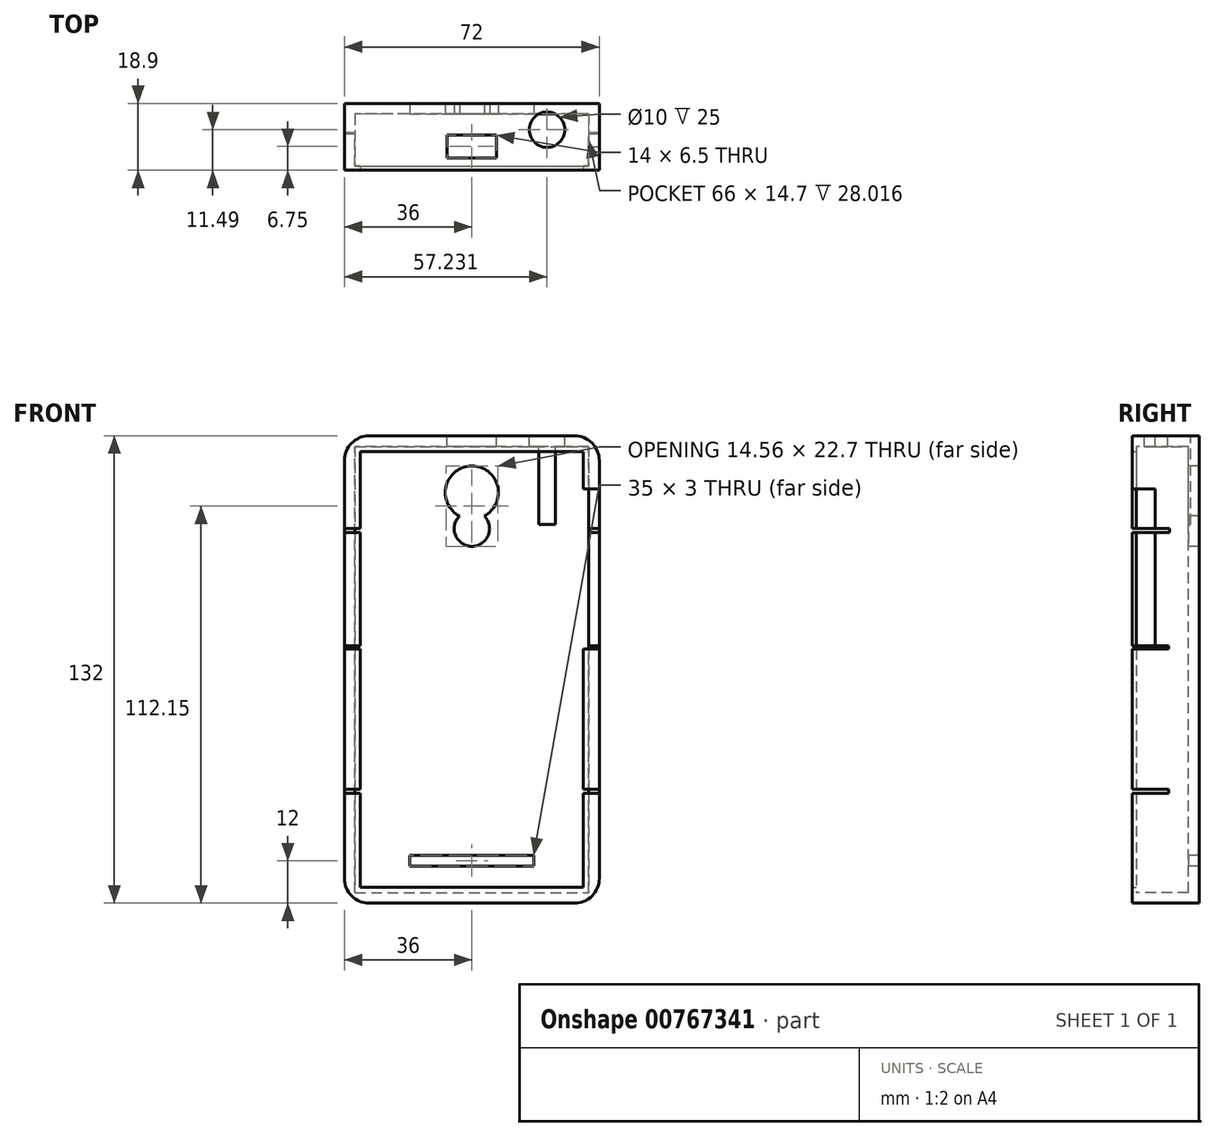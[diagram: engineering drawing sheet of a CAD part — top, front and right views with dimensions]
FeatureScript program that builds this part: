
annotation { "Feature Type Name" : "Feature", "Feature Type Description" : "" }
export const myFeature = defineFeature(function(context is Context, id is Id, definition is map)
    precondition{}
    {
        {
            var Q0;
            Q0=qCreatedBy(makeId("Front.planeOp"),FACE);
            var sketch = newSketch(context, id + "F0", { "sketchPlane" : qUnion([Q0])});
            skPoint(sketch, "E0.0", {"position": v(0, 0) * mm});
            skLineSegment(sketch, "E1.bottom", {"start": v(-36, 66) * mm, "end": v(36, 66) * mm});
            skLineSegment(sketch, "E1.top", {"start": v(-36, -66) * mm, "end": v(36, -66) * mm});
            skLineSegment(sketch, "E1.left", {"start": v(-36, 66) * mm, "end": v(-36, -66) * mm});
            skLineSegment(sketch, "E1.right", {"start": v(36, 66) * mm, "end": v(36, -66) * mm});
            skSolve(sketch);
        }
        {
            var Q0;
            Q0=makeQuery(id+"F0.imprint","IMPRINT",FACE,{"disambiguationData":[TD([[makeQuery(id+"F0.imprint","IMPRINT",EDGE,{"derivedFrom":sQuery(id+"F0.wireOp",EDGE,"E1.bottom")}),-1.0]])]});
            extrude(context, id + "F1", {"entities" : qUnion([Q0]), "depth" : 17.7 * mm, "offsetDistance" : 25 * mm});
        }
        {
            var Q0;
            Q0=makeQuery(id+"F1.opExtrude","CAP_FACE",FACE,{"disambiguationData":[OSD([sQuery(id+"F0.wireOp",EDGE,"E1.bottom"),sQuery(id+"F0.wireOp",EDGE,"E1.top"),sQuery(id+"F0.wireOp",EDGE,"E1.left"),sQuery(id+"F0.wireOp",EDGE,"E1.right")])],"isStart":false});
            var sketch = newSketch(context, id + "F2", { "sketchPlane" : qUnion([Q0])});
            skLineSegment(sketch, "E2.bottom", {"start": v(-33, 63) * mm, "end": v(33, 63) * mm});
            skLineSegment(sketch, "E2.top", {"start": v(-33, -63) * mm, "end": v(33, -63) * mm});
            skLineSegment(sketch, "E2.left", {"start": v(-33, 63) * mm, "end": v(-33, -63) * mm});
            skLineSegment(sketch, "E2.right", {"start": v(33, 63) * mm, "end": v(33, -63) * mm});
            skSolve(sketch);
        }
        {
            var Q0;
            Q0=makeQuery(id+"F2.imprint","IMPRINT",FACE,{"disambiguationData":[TD([[makeQuery(id+"F2.imprint","IMPRINT",EDGE,{"derivedFrom":sQuery(id+"F2.wireOp",EDGE,"E2.bottom")}),-1.0]])]});
            var Q1;
            Q1=makeQuery(id+"F1.opExtrude","CAP_FACE",FACE,{"disambiguationData":[OSD([sQuery(id+"F0.wireOp",EDGE,"E1.bottom"),sQuery(id+"F0.wireOp",EDGE,"E1.top"),sQuery(id+"F0.wireOp",EDGE,"E1.left"),sQuery(id+"F0.wireOp",EDGE,"E1.right")])],"isStart":true});
            extrude(context, id + "F3", {"entities" : qUnion([Q0]), "operationType" : NewBodyOperationType.REMOVE, "endBound" : BoundingType.UP_TO_SURFACE, "oppositeDirection" : true, "depth" : 8.5 * mm, "endBoundEntityFace" : qUnion([Q1]), "hasOffset" : true, "offsetDistance" : 3 * mm});
        }
        {
            var Q0;
            Q0=makeQuery(id+"F1.opExtrude","CAP_FACE",FACE,{"disambiguationData":[OSD([sQuery(id+"F0.wireOp",EDGE,"E1.bottom"),sQuery(id+"F0.wireOp",EDGE,"E1.top"),sQuery(id+"F0.wireOp",EDGE,"E1.left"),sQuery(id+"F0.wireOp",EDGE,"E1.right")])],"isStart":false});
            var sketch = newSketch(context, id + "F4", { "sketchPlane" : qUnion([Q0])});
            skLineSegment(sketch, "E3.bottom", {"start": v(-31.5, 61.5) * mm, "end": v(31.5, 61.5) * mm});
            skLineSegment(sketch, "E3.top", {"start": v(-31.5, -61.5) * mm, "end": v(31.5, -61.5) * mm});
            skLineSegment(sketch, "E3.left", {"start": v(-31.5, 61.5) * mm, "end": v(-31.5, -61.5) * mm});
            skLineSegment(sketch, "E3.right", {"start": v(31.5, 61.5) * mm, "end": v(31.5, -61.5) * mm});
            skSolve(sketch);
        }
        {
            var Q0;
            Q0=makeQuery(id+"F4.imprint","IMPRINT",FACE,{"disambiguationData":[TD([[makeQuery(id+"F4.imprint","IMPRINT",EDGE,{"derivedFrom":sQuery(id+"F4.wireOp",EDGE,"E3.bottom")}),1.0]])]});
            var Q1;
            Q1=makeQuery(id+"F4.imprint","IMPRINT",FACE,{"disambiguationData":[TD([[makeQuery(id+"F4.imprint","IMPRINT",EDGE,{"derivedFrom":makeQuery(id+"F1.opExtrude","CAP_EDGE",EDGE,{"disambiguationData":[OSD([sQuery(id+"F0.wireOp",EDGE,"E1.bottom")])],"isStart":false})}),-1.0]])]});
            extrude(context, id + "F5", {"entities" : qUnion([Q0, Q1]), "operationType" : NewBodyOperationType.ADD, "depth" : 1.2 * mm, "offsetDistance" : 25 * mm});
        }
        {
            var Q0;
            Q0=makeQuery(id+"F3.boolean.opBoolean","COPY",FACE,{"derivedFrom":makeQuery(id+"F3.opExtrude","CAP_FACE",FACE,{"disambiguationData":[OSD([sQuery(id+"F2.wireOp",EDGE,"E2.bottom"),sQuery(id+"F2.wireOp",EDGE,"E2.top"),sQuery(id+"F2.wireOp",EDGE,"E2.left"),sQuery(id+"F2.wireOp",EDGE,"E2.right")])],"isStart":false})});
            var sketch = newSketch(context, id + "F6", { "sketchPlane" : qUnion([Q0])});
            skCircle(sketch, "E4", {"center": v(0, 50) * mm, "radius": 7.5 * mm});
            skSolve(sketch);
        }
        {
            var Q0;
            Q0=makeQuery(id+"F6.imprint","IMPRINT",FACE,{"disambiguationData":[TD([[makeQuery(id+"F6.imprint","IMPRINT",EDGE,{"derivedFrom":sQuery(id+"F6.wireOp",EDGE,"E4")}),1.0]])]});
            extrude(context, id + "F7", {"entities" : qUnion([Q0]), "operationType" : NewBodyOperationType.REMOVE, "oppositeDirection" : true, "depth" : 25 * mm, "offsetDistance" : 25 * mm});
        }
        {
            var Q0;
            Q0 = qSketchRegion(id + "F6", true);
            extrude(context, id + "F8", {"entities" : qUnion([Q0]), "operationType" : NewBodyOperationType.REMOVE, "oppositeDirection" : true, "depth" : 25 * mm, "offsetDistance" : 25 * mm});
        }
        {
            var Q0;
            Q0=makeQuery(id+"F3.boolean.opBoolean","COPY",FACE,{"derivedFrom":makeQuery(id+"F3.opExtrude","CAP_FACE",FACE,{"disambiguationData":[OSD([sQuery(id+"F2.wireOp",EDGE,"E2.bottom"),sQuery(id+"F2.wireOp",EDGE,"E2.top"),sQuery(id+"F2.wireOp",EDGE,"E2.left"),sQuery(id+"F2.wireOp",EDGE,"E2.right")])],"isStart":false})});
            var sketch = newSketch(context, id + "F9", { "sketchPlane" : qUnion([Q0])});
            skCircle(sketch, "E5", {"center": v(0, 39.8) * mm, "radius": 5 * mm});
            skSolve(sketch);
        }
        {
            var Q0;
            Q0 = qSketchRegion(id + "F9", true);
            extrude(context, id + "F10", {"entities" : qUnion([Q0]), "operationType" : NewBodyOperationType.REMOVE, "oppositeDirection" : true, "depth" : 25 * mm, "offsetDistance" : 25 * mm});
        }
        {
            var Q0;
            {var subQ0=sQuery(id+"F0.wireOp",EDGE,"E1.bottom");Q0=makeQuery(id+"F5.boolean.opBoolean","MERGE",FACE,{"derivedFrom":[makeQuery(id+"F1.opExtrude","SWEPT_FACE",FACE,{"disambiguationData":[OSD([subQ0])]}),makeQuery(id+"F5.opExtrude","SWEPT_FACE",FACE,{"disambiguationData":[OSD([subQ0])]})]});}
            var sketch = newSketch(context, id + "F11", { "sketchPlane" : qUnion([Q0])});
            skLineSegment(sketch, "E6.bottom", {"start": v(-7, -8.9) * mm, "end": v(7, -8.9) * mm});
            skLineSegment(sketch, "E6.top", {"start": v(-7, -15.4) * mm, "end": v(7, -15.4) * mm});
            skLineSegment(sketch, "E6.left", {"start": v(-7, -8.9) * mm, "end": v(-7, -15.4) * mm});
            skLineSegment(sketch, "E6.right", {"start": v(7, -8.9) * mm, "end": v(7, -15.4) * mm});
            skSolve(sketch);
        }
        {
            var Q0;
            Q0 = qSketchRegion(id + "F11", true);
            extrude(context, id + "F12", {"entities" : qUnion([Q0]), "operationType" : NewBodyOperationType.REMOVE, "oppositeDirection" : true, "depth" : 25 * mm, "offsetDistance" : 25 * mm});
        }
        {
            var Q0;
            Q0=makeQuery(id+"F3.boolean.opBoolean","COPY",FACE,{"derivedFrom":makeQuery(id+"F3.opExtrude","CAP_FACE",FACE,{"disambiguationData":[OSD([sQuery(id+"F2.wireOp",EDGE,"E2.bottom"),sQuery(id+"F2.wireOp",EDGE,"E2.top"),sQuery(id+"F2.wireOp",EDGE,"E2.left"),sQuery(id+"F2.wireOp",EDGE,"E2.right")])],"isStart":false})});
            var sketch = newSketch(context, id + "F13", { "sketchPlane" : qUnion([Q0])});
            skLineSegment(sketch, "E7.bottom", {"start": v(-17.5, -52.5) * mm, "end": v(17.5, -52.5) * mm});
            skLineSegment(sketch, "E7.top", {"start": v(-17.5, -55.5) * mm, "end": v(17.5, -55.5) * mm});
            skLineSegment(sketch, "E7.left", {"start": v(-17.5, -52.5) * mm, "end": v(-17.5, -55.5) * mm});
            skLineSegment(sketch, "E7.right", {"start": v(17.5, -52.5) * mm, "end": v(17.5, -55.5) * mm});
            skSolve(sketch);
        }
        {
            var Q0;
            Q0=makeQuery(id+"F13.imprint","IMPRINT",FACE,{"disambiguationData":[TD([[makeQuery(id+"F13.imprint","IMPRINT",EDGE,{"derivedFrom":sQuery(id+"F13.wireOp",EDGE,"E7.bottom")}),-1.0]])]});
            extrude(context, id + "F14", {"entities" : qUnion([Q0]), "operationType" : NewBodyOperationType.REMOVE, "oppositeDirection" : true, "depth" : 25 * mm, "offsetDistance" : 25 * mm});
        }
        {
            var Q0;
            {var subQ0=sQuery(id+"F0.wireOp",EDGE,"E1.right");Q0=makeQuery(id+"F5.boolean.opBoolean","MERGE",FACE,{"derivedFrom":[makeQuery(id+"F1.opExtrude","SWEPT_FACE",FACE,{"disambiguationData":[OSD([subQ0])]}),makeQuery(id+"F5.opExtrude","SWEPT_FACE",FACE,{"disambiguationData":[OSD([subQ0])]})]});}
            var sketch = newSketch(context, id + "F15", { "sketchPlane" : qUnion([Q0])});
            skLineSegment(sketch, "E8.bottom", {"start": v(-18.9, 51) * mm, "end": v(-12.4, 51) * mm});
            skLineSegment(sketch, "E8.top", {"start": v(-18.9, 6) * mm, "end": v(-12.4, 6) * mm});
            skLineSegment(sketch, "E8.left", {"start": v(-18.9, 51) * mm, "end": v(-18.9, 6) * mm});
            skLineSegment(sketch, "E8.right", {"start": v(-12.4, 51) * mm, "end": v(-12.4, 6) * mm});
            skSolve(sketch);
        }
        {
            var Q0;
            Q0=makeQuery(id+"F15.imprint","IMPRINT",FACE,{"disambiguationData":[TD([[makeQuery(id+"F15.imprint","IMPRINT",EDGE,{"derivedFrom":sQuery(id+"F15.wireOp",EDGE,"E8.bottom")}),-1.0]])]});
            extrude(context, id + "F16", {"entities" : qUnion([Q0]), "operationType" : NewBodyOperationType.REMOVE, "oppositeDirection" : true, "depth" : 25 * mm, "offsetDistance" : 25 * mm});
        }
        {
            var Q0;
            {var subQ0=sQuery(id+"F0.wireOp",EDGE,"E1.bottom");Q0=makeQuery(id+"F5.boolean.opBoolean","MERGE",FACE,{"derivedFrom":[makeQuery(id+"F1.opExtrude","SWEPT_FACE",FACE,{"disambiguationData":[OSD([subQ0])]}),makeQuery(id+"F5.opExtrude","SWEPT_FACE",FACE,{"disambiguationData":[OSD([subQ0])]})]});}
            var sketch = newSketch(context, id + "F17", { "sketchPlane" : qUnion([Q0])});
            skCircle(sketch, "E9", {"center": v(21.23, -7.4) * mm, "radius": 5 * mm});
            skSolve(sketch);
        }
        {
            var Q0;
            Q0=makeQuery(id+"F17.imprint","IMPRINT",FACE,{"disambiguationData":[TD([[makeQuery(id+"F17.imprint","IMPRINT",EDGE,{"derivedFrom":sQuery(id+"F17.wireOp",EDGE,"E9")}),1.0]])]});
            extrude(context, id + "F18", {"entities" : qUnion([Q0]), "operationType" : NewBodyOperationType.REMOVE, "oppositeDirection" : true, "depth" : 25 * mm, "offsetDistance" : 25 * mm});
        }
        {
            var Q0;
            {var subQ0=sQuery(id+"F0.wireOp",EDGE,"E1.left");var subQ1=sQuery(id+"F0.wireOp",EDGE,"E1.bottom");Q0=makeQuery(id+"F5.boolean.opBoolean","MERGE",EDGE,{"derivedFrom":[makeQuery(id+"F1.opExtrude","SWEPT_EDGE",EDGE,{"disambiguationData":[OSD([subQ1,subQ0])]}),makeQuery(id+"F5.opExtrude","SWEPT_EDGE",EDGE,{"disambiguationData":[OSD([subQ1,subQ0])]})]});}
            var Q1;
            {var subQ0=sQuery(id+"F0.wireOp",EDGE,"E1.right");var subQ1=sQuery(id+"F0.wireOp",EDGE,"E1.bottom");Q1=makeQuery(id+"F5.boolean.opBoolean","MERGE",EDGE,{"derivedFrom":[makeQuery(id+"F1.opExtrude","SWEPT_EDGE",EDGE,{"disambiguationData":[OSD([subQ1,subQ0])]}),makeQuery(id+"F5.opExtrude","SWEPT_EDGE",EDGE,{"disambiguationData":[OSD([subQ1,subQ0])]})]});}
            var Q2;
            {var subQ0=sQuery(id+"F0.wireOp",EDGE,"E1.left");var subQ1=sQuery(id+"F0.wireOp",EDGE,"E1.top");Q2=makeQuery(id+"F5.boolean.opBoolean","MERGE",EDGE,{"derivedFrom":[makeQuery(id+"F1.opExtrude","SWEPT_EDGE",EDGE,{"disambiguationData":[OSD([subQ1,subQ0])]}),makeQuery(id+"F5.opExtrude","SWEPT_EDGE",EDGE,{"disambiguationData":[OSD([subQ1,subQ0])]})]});}
            var Q3;
            {var subQ0=sQuery(id+"F0.wireOp",EDGE,"E1.right");var subQ1=sQuery(id+"F0.wireOp",EDGE,"E1.top");Q3=makeQuery(id+"F5.boolean.opBoolean","MERGE",EDGE,{"derivedFrom":[makeQuery(id+"F1.opExtrude","SWEPT_EDGE",EDGE,{"disambiguationData":[OSD([subQ1,subQ0])]}),makeQuery(id+"F5.opExtrude","SWEPT_EDGE",EDGE,{"disambiguationData":[OSD([subQ1,subQ0])]})]});}
            fillet(context, id + "F19", {"entities" : qUnion([Q0, Q1, Q2, Q3]), "radius" : 7 * mm, "tangentPropagation" : true, "allowEdgeOverflow" : false});
        }
        {
            var Q0;
            {var subQ0=sQuery(id+"F0.wireOp",EDGE,"E1.left");Q0=makeQuery(id+"F5.boolean.opBoolean","MERGE",FACE,{"derivedFrom":[makeQuery(id+"F1.opExtrude","SWEPT_FACE",FACE,{"disambiguationData":[OSD([subQ0])]}),makeQuery(id+"F5.opExtrude","SWEPT_FACE",FACE,{"disambiguationData":[OSD([subQ0])]})]});}
            var sketch = newSketch(context, id + "F20", { "sketchPlane" : qUnion([Q0])});
            skLineSegment(sketch, "E10.bottom", {"start": v(18.9, 38.67) * mm, "end": v(8.36, 38.67) * mm});
            skLineSegment(sketch, "E10.top", {"start": v(18.9, 39.8) * mm, "end": v(8.36, 39.8) * mm});
            skLineSegment(sketch, "E10.left", {"start": v(18.9, 38.67) * mm, "end": v(18.9, 39.8) * mm});
            skLineSegment(sketch, "E10.right", {"start": v(8.36, 38.67) * mm, "end": v(8.36, 39.8) * mm});
            skLineSegment(sketch, "E11.bottom", {"start": v(18.9, 5.8) * mm, "end": v(8.64, 5.8) * mm});
            skLineSegment(sketch, "E11.top", {"start": v(18.9, 6.66) * mm, "end": v(8.64, 6.66) * mm});
            skLineSegment(sketch, "E11.left", {"start": v(18.9, 5.8) * mm, "end": v(18.9, 6.66) * mm});
            skLineSegment(sketch, "E11.right", {"start": v(8.64, 5.8) * mm, "end": v(8.64, 6.66) * mm});
            skLineSegment(sketch, "E12.bottom", {"start": v(18.9, -34.98) * mm, "end": v(8.64, -34.98) * mm});
            skLineSegment(sketch, "E12.top", {"start": v(18.9, -33.85) * mm, "end": v(8.64, -33.85) * mm});
            skLineSegment(sketch, "E12.left", {"start": v(18.9, -34.98) * mm, "end": v(18.9, -33.85) * mm});
            skLineSegment(sketch, "E12.right", {"start": v(8.64, -34.98) * mm, "end": v(8.64, -33.85) * mm});
            skSolve(sketch);
        }
        {
            var Q0;
            Q0 = qSketchRegion(id + "F20", true);
            extrude(context, id + "F21", {"entities" : qUnion([Q0]), "operationType" : NewBodyOperationType.REMOVE, "oppositeDirection" : true, "depth" : 81 * mm, "offsetDistance" : 25 * mm});
        }
    });
